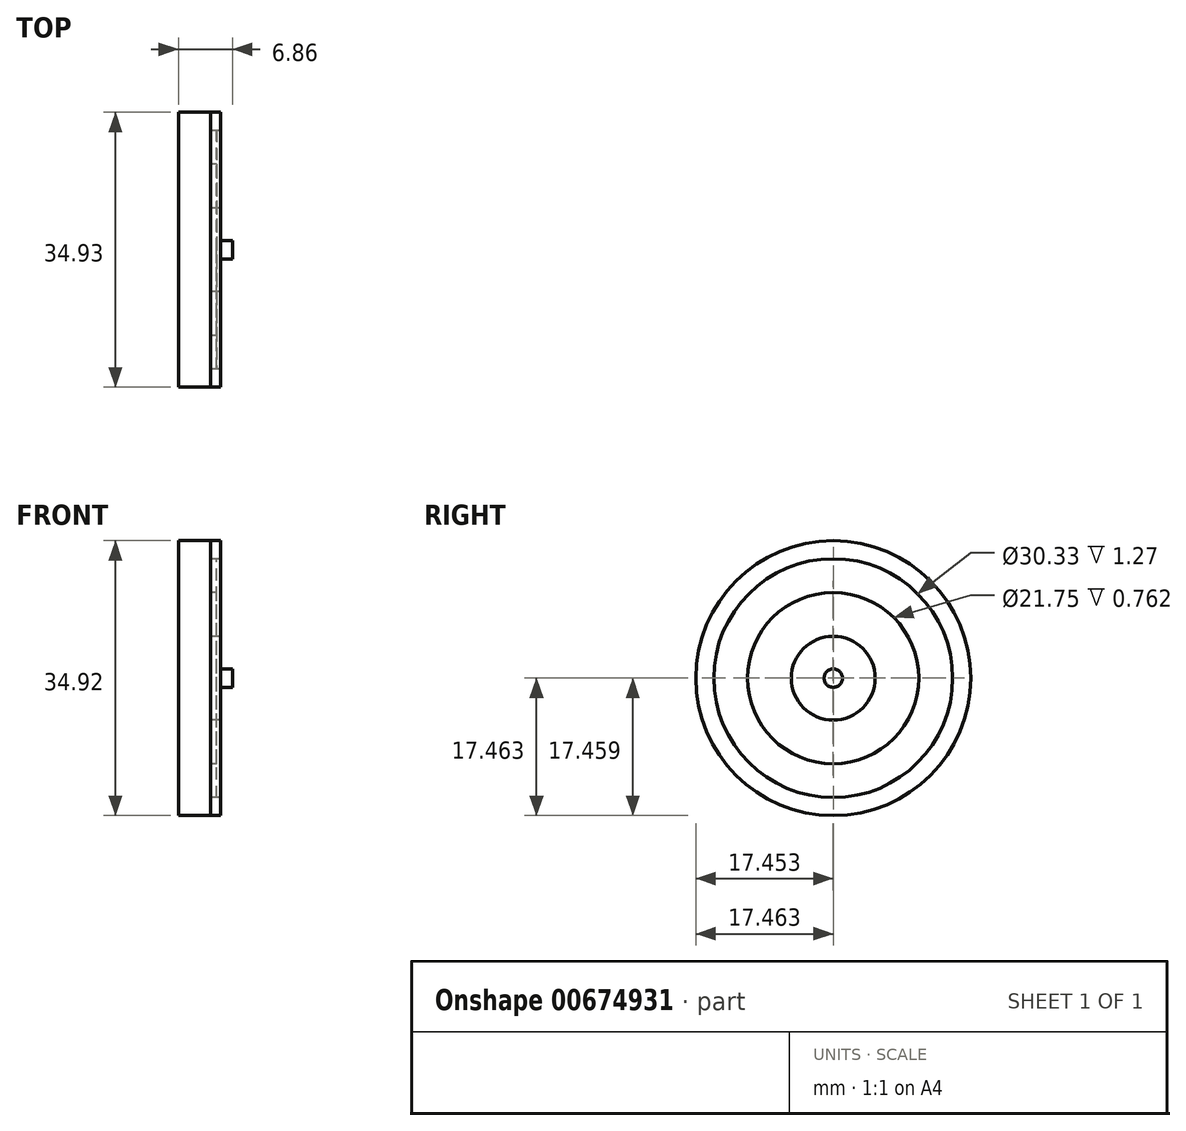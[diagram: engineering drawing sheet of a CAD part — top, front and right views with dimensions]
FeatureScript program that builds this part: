
annotation { "Feature Type Name" : "Feature", "Feature Type Description" : "" }
export const myFeature = defineFeature(function(context is Context, id is Id, definition is map)
    precondition{}
    {
        {
            var Q0;
            Q0=qCreatedBy(makeId("Right.planeOp"),FACE);
            var sketch = newSketch(context, id + "F0", { "sketchPlane" : qUnion([Q0])});
            skCircle(sketch, "E0", {"center": v(16.38, 19.94) * mm, "radius": 17.46 * mm});
            skSolve(sketch);
        }
        {
            var Q0;
            Q0=makeQuery(id+"F0.imprint","IMPRINT",FACE,{"disambiguationData":[TD([[makeQuery(id+"F0.imprint","IMPRINT",EDGE,{"derivedFrom":sQuery(id+"F0.wireOp",EDGE,"E0")}),1.0]])]});
            var sketch = newSketch(context, id + "F1", { "sketchPlane" : qUnion([Q0])});
            skSolve(sketch);
        }
        {
            var Q0;
            Q0 = qSketchRegion(id + "F0", true);
            var Q1;
            Q1=makeQuery(id+"F1.imprint","IMPRINT",FACE,{"disambiguationData":[TD([[makeQuery(id+"F1.imprint","IMPRINT",EDGE,{"derivedFrom":makeQuery(id+"F0.imprint","IMPRINT",EDGE,{"derivedFrom":sQuery(id+"F0.wireOp",EDGE,"E0")})}),1.0]])]});
            extrude(context, id + "F2", {"entities" : qUnion([Q0, Q1]), "depth" : 4.06 * mm, "offsetDistance" : 25.4 * mm});
        }
        {
            var Q0;
            {var subQ0=sQuery(id+"F0.wireOp",EDGE,"E0");Q0=makeQuery(id+"F2.opExtrude","CAP_FACE",FACE,{"disambiguationData":[OSD([subQ0]),TDD([makeQuery(id+"F0.imprint","IMPRINT",EDGE,{"derivedFrom":subQ0})])],"isStart":false});}
            var sketch = newSketch(context, id + "F3", { "sketchPlane" : qUnion([Q0])});
            skCircle(sketch, "E1", {"center": v(16.38, 19.94) * mm, "radius": 15.17 * mm});
            skSolve(sketch);
        }
        {
            var Q0;
            Q0=makeQuery(id+"F3.imprint","IMPRINT",FACE,{"disambiguationData":[TD([[makeQuery(id+"F3.imprint","IMPRINT",EDGE,{"derivedFrom":sQuery(id+"F3.wireOp",EDGE,"E1")}),-1.0]])]});
            var sketch = newSketch(context, id + "F4", { "sketchPlane" : qUnion([Q0])});
            skCircle(sketch, "E2", {"center": v(16.37, 19.94) * mm, "radius": 10.87 * mm});
            skSolve(sketch);
        }
        {
            var Q0;
            Q0=makeQuery(id+"F3.imprint","IMPRINT",FACE,{"disambiguationData":[TD([[makeQuery(id+"F3.imprint","IMPRINT",EDGE,{"derivedFrom":sQuery(id+"F3.wireOp",EDGE,"E1")}),-1.0]])]});
            var sketch = newSketch(context, id + "F5", { "sketchPlane" : qUnion([Q0])});
            skCircle(sketch, "E3", {"center": v(16.35, 19.95) * mm, "radius": 10.04 * mm});
            skSolve(sketch);
        }
        {
            var Q0;
            Q0=makeQuery(id+"F4.imprint","IMPRINT",FACE,{"disambiguationData":[TD([[makeQuery(id+"F4.imprint","IMPRINT",EDGE,{"derivedFrom":sQuery(id+"F4.wireOp",EDGE,"E2")}),-1.0]])]});
            extrude(context, id + "F6", {"entities" : qUnion([Q0]), "depth" : 0.76 * mm, "offsetDistance" : 25.4 * mm});
        }
        {
            var Q0;
            Q0=makeQuery(id+"F5.imprint","IMPRINT",FACE,{"disambiguationData":[TD([[makeQuery(id+"F5.imprint","IMPRINT",EDGE,{"derivedFrom":sQuery(id+"F5.wireOp",EDGE,"E3")}),1.0]])]});
            var sketch = newSketch(context, id + "F7", { "sketchPlane" : qUnion([Q0])});
            skCircle(sketch, "E4", {"center": v(16.38, 19.94) * mm, "radius": 5.32 * mm});
            skSolve(sketch);
        }
        {
            var Q0;
            Q0=makeQuery(id+"F7.imprint","IMPRINT",FACE,{"disambiguationData":[TD([[makeQuery(id+"F7.imprint","IMPRINT",EDGE,{"derivedFrom":sQuery(id+"F7.wireOp",EDGE,"E4")}),1.0]])]});
            var Q1;
            Q1=makeQuery(id+"F5.imprint","IMPRINT",FACE,{"disambiguationData":[TD([[makeQuery(id+"F5.imprint","IMPRINT",EDGE,{"derivedFrom":makeQuery(id+"F3.imprint","IMPRINT",EDGE,{"derivedFrom":sQuery(id+"F3.wireOp",EDGE,"E1")})}),-1.0]])]});
            extrude(context, id + "F8", {"entities" : qUnion([Q0, Q1]), "depth" : 1.27 * mm, "offsetDistance" : 25.4 * mm});
        }
        {
            var Q0;
            Q0=makeQuery(id+"F8.opExtrude","CAP_FACE",FACE,{"disambiguationData":[OSD([sQuery(id+"F7.wireOp",EDGE,"E4")])],"isStart":false});
            var sketch = newSketch(context, id + "F9", { "sketchPlane" : qUnion([Q0])});
            skCircle(sketch, "E5", {"center": v(16.38, 19.94) * mm, "radius": 1.16 * mm});
            skSolve(sketch);
        }
        {
            var Q0;
            Q0=makeQuery(id+"F9.imprint","IMPRINT",FACE,{"disambiguationData":[TD([[makeQuery(id+"F9.imprint","IMPRINT",EDGE,{"derivedFrom":sQuery(id+"F9.wireOp",EDGE,"E5")}),1.0]])]});
            extrude(context, id + "F10", {"entities" : qUnion([Q0]), "operationType" : NewBodyOperationType.ADD, "depth" : 1.52 * mm, "offsetDistance" : 25.4 * mm});
        }
    });
